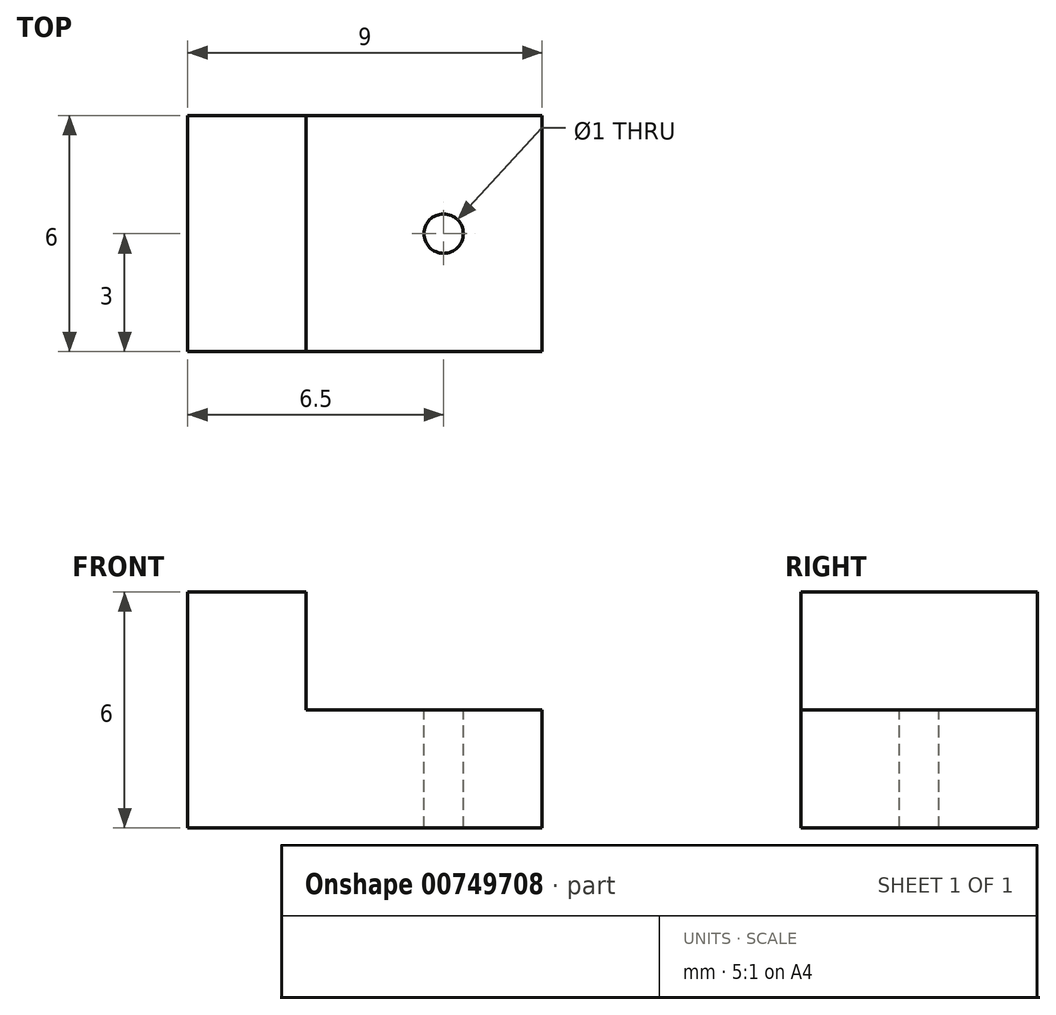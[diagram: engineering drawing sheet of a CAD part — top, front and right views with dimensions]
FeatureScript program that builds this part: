
annotation { "Feature Type Name" : "Feature", "Feature Type Description" : "" }
export const myFeature = defineFeature(function(context is Context, id is Id, definition is map)
    precondition{}
    {
        {
            var Q0;
            Q0=qCreatedBy(makeId("Front.planeOp"),FACE);
            var sketch = newSketch(context, id + "F0", { "sketchPlane" : qUnion([Q0])});
            skLineSegment(sketch, "E0.bottom", {"start": v(0, 0) * mm, "end": v(9, 0) * mm});
            skLineSegment(sketch, "E0.top", {"start": v(0, 6) * mm, "end": v(9, 6) * mm});
            skLineSegment(sketch, "E0.left", {"start": v(0, 0) * mm, "end": v(0, 6) * mm});
            skLineSegment(sketch, "E0.right", {"start": v(9, 0) * mm, "end": v(9, 6) * mm});
            skSolve(sketch);
        }
        {
            var Q0;
            Q0 = qSketchRegion(id + "F0", true);
            extrude(context, id + "F1", {"entities" : qUnion([Q0]), "depth" : 6 * mm, "offsetDistance" : 25 * mm});
        }
        {
            var Q0;
            Q0=makeQuery(id+"F1.opExtrude","SWEPT_FACE",FACE,{"disambiguationData":[OSD([sQuery(id+"F0.wireOp",EDGE,"E0.top")])]});
            var sketch = newSketch(context, id + "F2", { "sketchPlane" : qUnion([Q0])});
            skLineSegment(sketch, "E1", {"start": v(3, 0) * mm, "end": v(3, -6) * mm});
            skSolve(sketch);
        }
        {
            var Q0;
            Q0 = qSketchRegion(id + "F2", true);
            var Q1;
            {var subQ0=sQuery(id+"F2.wireOp",EDGE,"E1");Q1=makeQuery(id+"F2.imprint","IMPRINT",FACE,{"disambiguationData":[TD([[makeQuery(id+"F2.imprint","IMPRINT",EDGE,{"derivedFrom":subQ0}),1.0]])]});}
            extrude(context, id + "F3", {"entities" : qUnion([Q0, Q1]), "operationType" : NewBodyOperationType.REMOVE, "oppositeDirection" : true, "depth" : 3 * mm, "offsetDistance" : 25 * mm});
        }
        {
            var Q0;
            Q0=makeQuery(id+"F3.boolean.opBoolean","COPY",FACE,{"derivedFrom":makeQuery(id+"F3.opExtrude","CAP_FACE",FACE,{"disambiguationData":[OSD([sQuery(id+"F0.wireOp",EDGE,"E0.top"),sQuery(id+"F0.wireOp",EDGE,"E0.right"),sQuery(id+"F2.wireOp",EDGE,"E1")])],"isStart":false})});
            var sketch = newSketch(context, id + "F4", { "sketchPlane" : qUnion([Q0])});
            skCircle(sketch, "E2", {"center": v(6.5, -3) * mm, "radius": 0.5 * mm});
            skSolve(sketch);
        }
        {
            var Q0;
            Q0 = qSketchRegion(id + "F4", true);
            extrude(context, id + "F5", {"entities" : qUnion([Q0]), "operationType" : NewBodyOperationType.REMOVE, "oppositeDirection" : true, "depth" : 25 * mm, "offsetDistance" : 25 * mm});
        }
    });
